# Revit family: Sanext_Термостатический клапан SANEXT RV2,угловой
name_source: partatom
category: Арматура трубопроводов
revit_build: Autodesk Revit 2017 (Build: 20171027_0315(x64)
units: mm (PartAtom-declared; Revit-internal decimal feet)

## family parameters
Всегда вертикально = Да
На основе рабочей плоскости = Нет
Общий = Нет
При загрузке вырезать с полостями = Нет
Размер круглого соединителя = Использовать радиус
Тип детали = Клапан - Вставляется

## types (2) — shared parameters
ADSK_Единица измерения = шт
ADSK_Завод-изготовитель = ООО САНЕКСТ.ПРО
ADSK_Материал = DZR латунь
ADSK_Материал наименование = DZR латунь
URL = http://sanext.ru
h = 62 мм
z = 1
Диаметр.Крышка = 30 мм
Длина = 25 мм
Изготовитель = ООО САНЕКСТ.ПРО
Рабочее давление = 0.0 кПа
Разработчик = ООО ПРОРУБИМ
Разработчик (телефон) = +7(495)649-85-43
Разработчик модели (URL) = http://prorubim.com
zero-valued in all types: ADSK_Масса

## per-type parameters (varying)
| type | ADSK_Код изделия | ADSK_Наименование | ДиаметрКлапана | Описание | Радиус |
| Ду15 | 6612 | Термостатический клапан SANEXT RV2,угловой Ду15 | 15 мм | Термостатический клапан SANEXT RV2,угловой Ду15 | 8 мм |
| Ду20 | 6622 | Термостатический клапан SANEXT RV2,угловой Ду20 | 20 мм | Термостатический клапан SANEXT RV2,угловой Ду20 | 10 мм |
